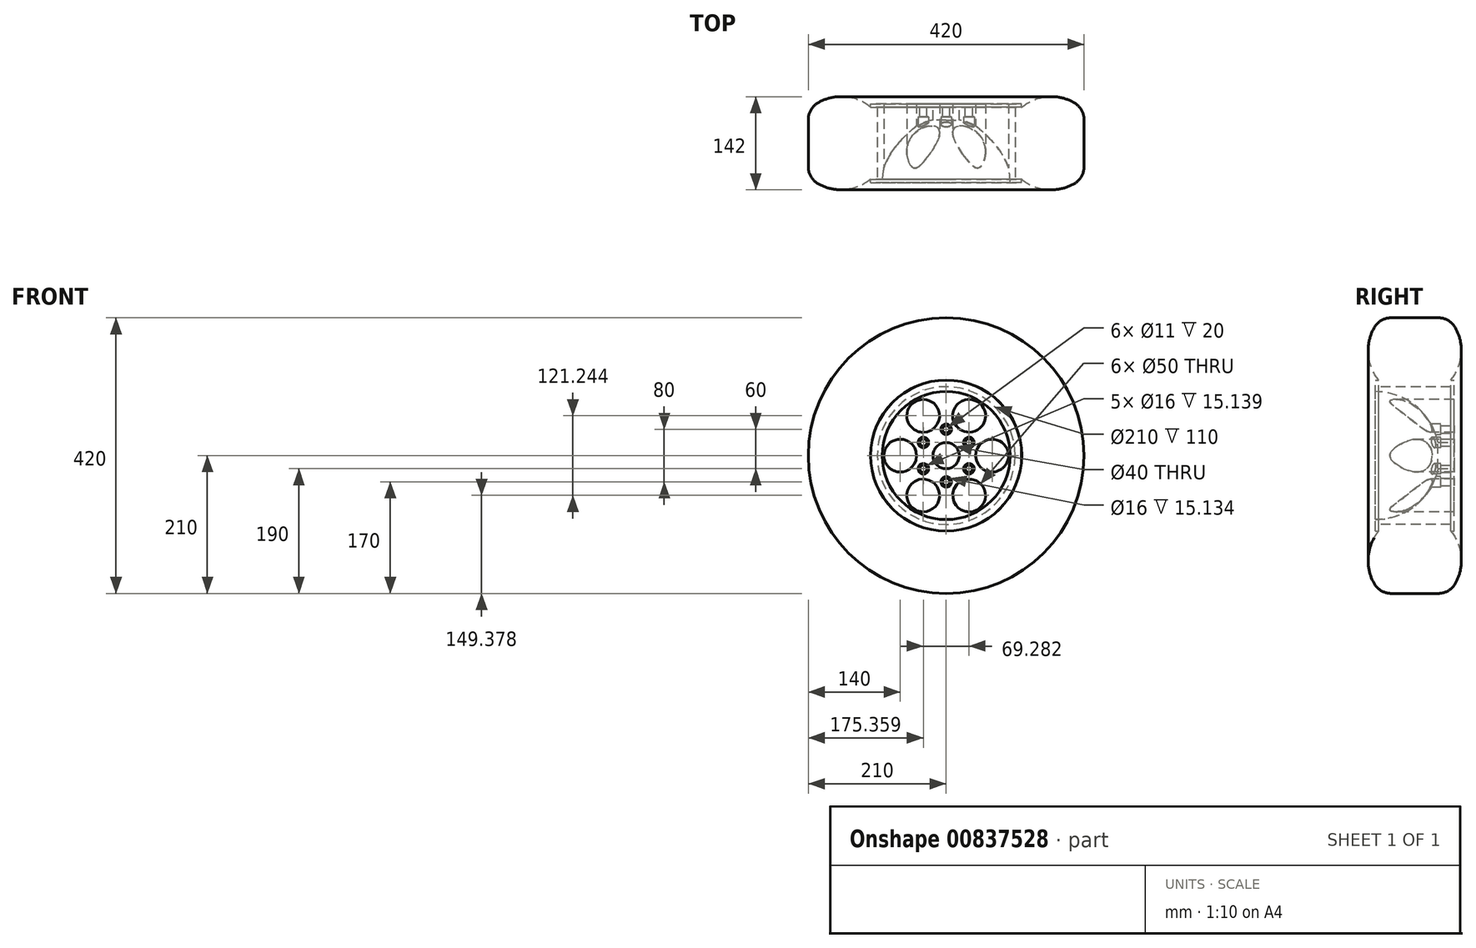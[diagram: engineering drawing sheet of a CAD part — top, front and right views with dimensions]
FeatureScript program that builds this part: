
annotation { "Feature Type Name" : "Feature", "Feature Type Description" : "" }
export const myFeature = defineFeature(function(context is Context, id is Id, definition is map)
    precondition{}
    {
        {
            var Q0;
            Q0=qCreatedBy(makeId("Front.planeOp"),FACE);
            var sketch = newSketch(context, id + "F0", { "sketchPlane" : qUnion([Q0])});
            skCircle(sketch, "E0", {"center": v(0, 0) * mm, "radius": 115 * mm});
            skSolve(sketch);
        }
        {
            var Q0;
            Q0 = qSketchRegion(id + "F0", true);
            extrude(context, id + "F1", {"entities" : qUnion([Q0]), "endBound" : BoundingType.SYMMETRIC, "depth" : 120 * mm, "offsetDistance" : 25 * mm});
        }
        {
            var Q0;
            Q0=qCreatedBy(makeId("Top.planeOp"),FACE);
            var sketch = newSketch(context, id + "F2", { "sketchPlane" : qUnion([Q0])});
            skLineSegment(sketch, "E1", {"start": v(0, 60) * mm, "end": v(0, -60) * mm, "construction": true});
            skArc(sketch, "E2", {"start": v(97.5, -60) * mm, "mid": v(68.94, 8.94) * mm, "end": v(0, 37.5) * mm});
            skLineSegment(sketch, "E3", {"start": v(0, -60) * mm, "end": v(97.5, -60) * mm});
            skLineSegment(sketch, "E4", {"start": v(0, -60) * mm, "end": v(0, 37.5) * mm});
            skSolve(sketch);
        }
        {
            var Q0;
            Q0 = qSketchRegion(id + "F2", true);
            var Q1;
            Q1=sQuery(id+"F2.wireOp",EDGE,"E1");
            revolve(context, id + "F3", {"operationType" : NewBodyOperationType.REMOVE, "surfaceOperationType" : NewSurfaceOperationType.NEW, "entities" : qUnion([Q0]), "axis" : qUnion([Q1]), "revolveType" : RevolveType.FULL, "oppositeDirection" : true});
        }
        {
            var Q0;
            Q0=qCreatedBy(makeId("Top.planeOp"),FACE);
            var sketch = newSketch(context, id + "F4", { "sketchPlane" : qUnion([Q0])});
            skLineSegment(sketch, "E5", {"start": v(0, 60) * mm, "end": v(0, -60) * mm, "construction": true});
            skLineSegment(sketch, "E6.bottom", {"start": v(105, 55) * mm, "end": v(120, 55) * mm});
            skLineSegment(sketch, "E6.top", {"start": v(105, -55) * mm, "end": v(120, -55) * mm});
            skLineSegment(sketch, "E6.left", {"start": v(105, 55) * mm, "end": v(105, -55) * mm});
            skLineSegment(sketch, "E6.right", {"start": v(120, 55) * mm, "end": v(120, -55) * mm});
            skSolve(sketch);
        }
        {
            var Q0;
            Q0=makeQuery(id+"F4.imprint","IMPRINT",FACE,{"disambiguationData":[TD([[makeQuery(id+"F4.imprint","IMPRINT",EDGE,{"derivedFrom":sQuery(id+"F4.wireOp",EDGE,"E6.bottom")}),-1.0]])]});
            var Q1;
            Q1=sQuery(id+"F4.wireOp",EDGE,"E5");
            revolve(context, id + "F5", {"operationType" : NewBodyOperationType.REMOVE, "surfaceOperationType" : NewSurfaceOperationType.NEW, "entities" : qUnion([Q0]), "axis" : qUnion([Q1]), "revolveType" : RevolveType.FULL, "oppositeDirection" : true});
        }
        {
            var Q0;
            Q0=makeQuery(id+"F1.opExtrude","CAP_FACE",FACE,{"disambiguationData":[OSD([sQuery(id+"F0.wireOp",EDGE,"E0")])],"isStart":true});
            var sketch = newSketch(context, id + "F6", { "sketchPlane" : qUnion([Q0])});
            skCircle(sketch, "E7", {"center": v(0, 0) * mm, "radius": 20 * mm});
            skSolve(sketch);
        }
        {
            var Q0;
            Q0 = qSketchRegion(id + "F6", true);
            extrude(context, id + "F7", {"entities" : qUnion([Q0]), "operationType" : NewBodyOperationType.REMOVE, "endBound" : BoundingType.UP_TO_NEXT, "oppositeDirection" : true, "depth" : 25 * mm, "offsetDistance" : 25 * mm});
        }
        {
            var Q0;
            Q0=makeQuery(id+"F1.opExtrude","CAP_FACE",FACE,{"disambiguationData":[OSD([sQuery(id+"F0.wireOp",EDGE,"E0")])],"isStart":true});
            var sketch = newSketch(context, id + "F8", { "sketchPlane" : qUnion([Q0])});
            skCircle(sketch, "E8", {"center": v(0, 0) * mm, "radius": 40 * mm, "construction": true});
            skCircle(sketch, "E9", {"center": v(0, 40) * mm, "radius": 5.5 * mm});
            skCircle(sketch, "E10.1.0", {"center": v(-34.64, 20) * mm, "radius": 5.5 * mm});
            skCircle(sketch, "E10.2.0", {"center": v(-34.64, -20) * mm, "radius": 5.5 * mm});
            skCircle(sketch, "E10.3.0", {"center": v(0, -40) * mm, "radius": 5.5 * mm});
            skCircle(sketch, "E10.4.0", {"center": v(34.64, -20) * mm, "radius": 5.5 * mm});
            skCircle(sketch, "E10.5.0", {"center": v(34.64, 20) * mm, "radius": 5.5 * mm});
            skSolve(sketch);
        }
        {
            var Q0;
            Q0 = qSketchRegion(id + "F8", true);
            extrude(context, id + "F9", {"entities" : qUnion([Q0]), "operationType" : NewBodyOperationType.REMOVE, "endBound" : BoundingType.UP_TO_NEXT, "oppositeDirection" : true, "depth" : 25 * mm, "offsetDistance" : 25 * mm});
        }
        {
            var Q0;
            Q0=makeQuery(id+"F1.opExtrude","CAP_FACE",FACE,{"disambiguationData":[OSD([sQuery(id+"F0.wireOp",EDGE,"E0")])],"isStart":false});
            var sketch = newSketch(context, id + "F10", { "sketchPlane" : qUnion([Q0])});
            skCircle(sketch, "E11", {"center": v(0, 0) * mm, "radius": 40 * mm, "construction": true});
            skCircle(sketch, "E12", {"center": v(0, 40) * mm, "radius": 8 * mm});
            skCircle(sketch, "E13.1.0", {"center": v(-34.64, 20) * mm, "radius": 8 * mm});
            skCircle(sketch, "E13.2.0", {"center": v(-34.64, -20) * mm, "radius": 8 * mm});
            skCircle(sketch, "E13.3.0", {"center": v(0, -40) * mm, "radius": 8 * mm});
            skCircle(sketch, "E13.4.0", {"center": v(34.64, -20) * mm, "radius": 8 * mm});
            skCircle(sketch, "E13.5.0", {"center": v(34.64, 20) * mm, "radius": 8 * mm});
            skSolve(sketch);
        }
        {
            var Q0;
            Q0 = qSketchRegion(id + "F10", true);
            extrude(context, id + "F11", {"entities" : qUnion([Q0]), "operationType" : NewBodyOperationType.REMOVE, "oppositeDirection" : true, "depth" : 100 * mm, "offsetDistance" : 25 * mm});
        }
        {
            var Q0;
            Q0=makeQuery(id+"F1.opExtrude","CAP_FACE",FACE,{"disambiguationData":[OSD([sQuery(id+"F0.wireOp",EDGE,"E0")])],"isStart":false});
            var sketch = newSketch(context, id + "F12", { "sketchPlane" : qUnion([Q0])});
            skCircle(sketch, "E14", {"center": v(0, 0) * mm, "radius": 70 * mm, "construction": true});
            skLineSegment(sketch, "E15", {"start": v(0, 0) * mm, "end": v(0, 70) * mm, "construction": true});
            skLineSegment(sketch, "E16", {"start": v(0, 0) * mm, "end": v(-35, 60.62) * mm, "construction": true});
            skCircle(sketch, "E17", {"center": v(-35, 60.62) * mm, "radius": 25 * mm});
            skCircle(sketch, "E18.1.0", {"center": v(-70, 0) * mm, "radius": 25 * mm});
            skCircle(sketch, "E18.2.0", {"center": v(-35, -60.62) * mm, "radius": 25 * mm});
            skCircle(sketch, "E18.3.0", {"center": v(35, -60.62) * mm, "radius": 25 * mm});
            skCircle(sketch, "E18.4.0", {"center": v(70, 0) * mm, "radius": 25 * mm});
            skCircle(sketch, "E18.5.0", {"center": v(35, 60.62) * mm, "radius": 25 * mm});
            skSolve(sketch);
        }
        {
            var Q0;
            Q0 = qSketchRegion(id + "F12", true);
            extrude(context, id + "F13", {"entities" : qUnion([Q0]), "operationType" : NewBodyOperationType.REMOVE, "oppositeDirection" : true, "depth" : 130 * mm, "offsetDistance" : 25 * mm});
        }
        {
            var Q0;
            Q0=qCreatedBy(makeId("Top.planeOp"),FACE);
            var sketch = newSketch(context, id + "F14", { "sketchPlane" : qUnion([Q0])});
            skLineSegment(sketch, "E19", {"start": v(0, 0) * mm, "end": v(0, 60) * mm, "construction": true});
            skLineSegment(sketch, "E20.bottom", {"start": v(105, 55) * mm, "end": v(115.1, 55) * mm});
            skLineSegment(sketch, "E20.top", {"start": v(105, -55) * mm, "end": v(115.1, -55) * mm});
            skLineSegment(sketch, "E20.left", {"start": v(105, 55) * mm, "end": v(105, -55) * mm});
            skLineSegment(sketch, "E21", {"start": v(0, 0) * mm, "end": v(160, 0) * mm, "construction": true});
            skArc(sketch, "E22", {"start": v(115.1, -55) * mm, "mid": v(153.8, -70.73) * mm, "end": v(194.63, -61.98) * mm});
            skLineSegment(sketch, "E23", {"start": v(210, 35.8) * mm, "end": v(210, -35.8) * mm});
            skArc(sketch, "E24.trimOffspring", {"start": v(194.63, 61.98) * mm, "mid": v(153.8, 70.73) * mm, "end": v(115.1, 55) * mm});
            skPoint(sketch, "E25.visualSharp", {"position": v(210, 50.4) * mm});
            skArc(sketch, "E25.filletArc", {"start": v(210, 35.8) * mm, "mid": v(205.87, 50.97) * mm, "end": v(194.63, 61.98) * mm});
            skPoint(sketch, "E26.visualSharp", {"position": v(210, -50.4) * mm});
            skArc(sketch, "E26.filletArc", {"start": v(194.63, -61.98) * mm, "mid": v(205.87, -50.97) * mm, "end": v(210, -35.8) * mm});
            skSolve(sketch);
        }
        {
            var Q0;
            Q0 = qSketchRegion(id + "F14", true);
            var Q1;
            Q1=sQuery(id+"F14.wireOp",EDGE,"E19");
            revolve(context, id + "F15", {"surfaceOperationType" : NewSurfaceOperationType.NEW, "entities" : qUnion([Q0]), "axis" : qUnion([Q1]), "revolveType" : RevolveType.FULL});
        }
    });
